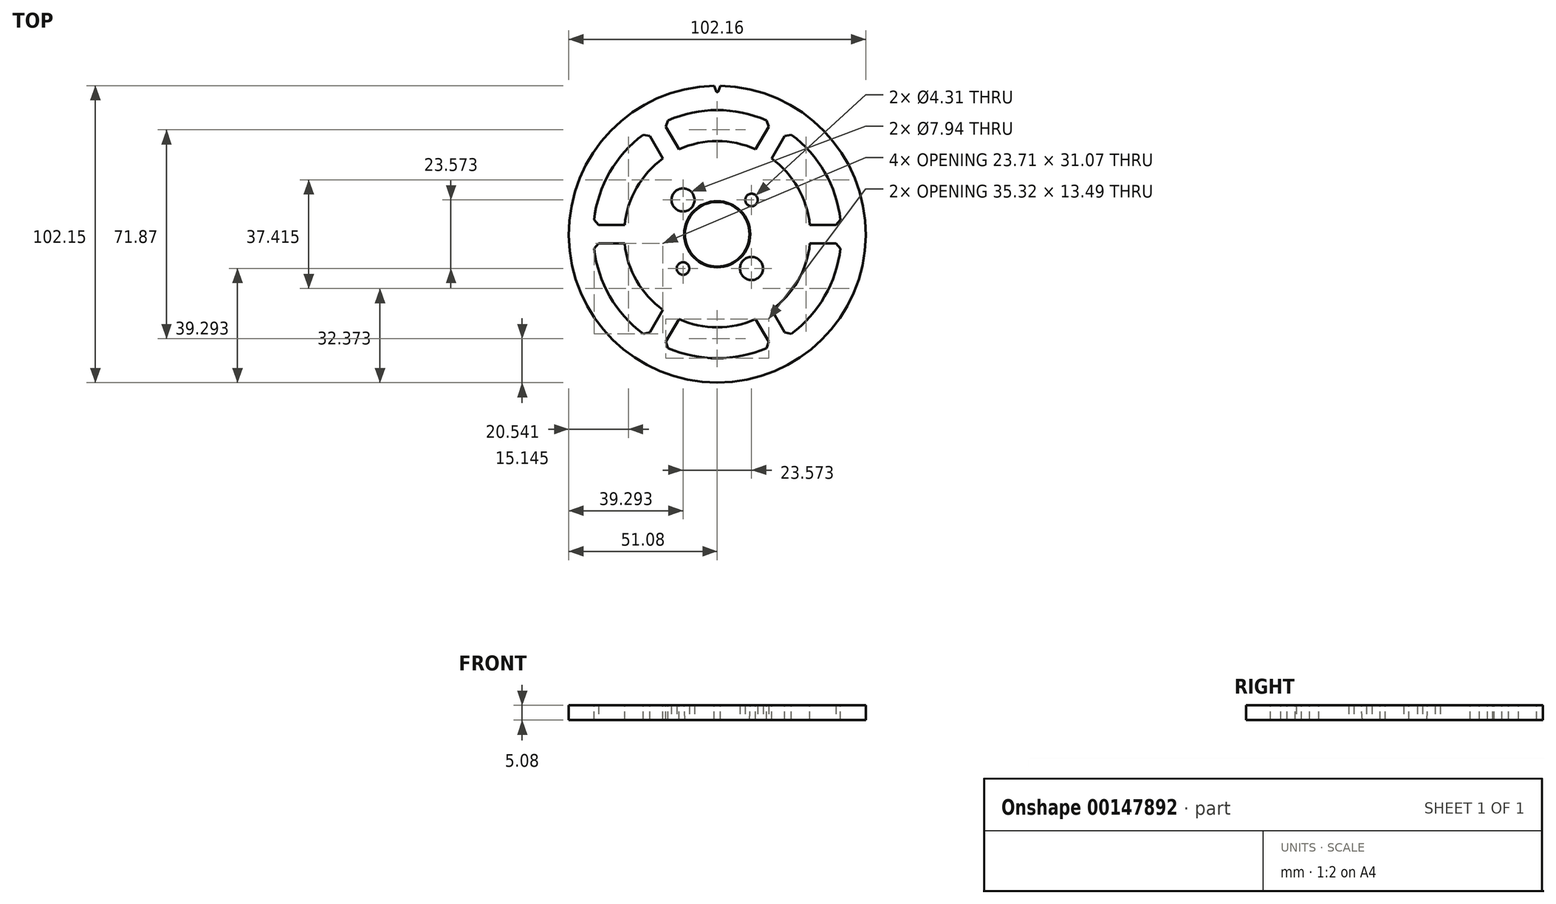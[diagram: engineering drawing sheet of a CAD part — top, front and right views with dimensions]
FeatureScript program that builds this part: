
annotation { "Feature Type Name" : "Feature", "Feature Type Description" : "" }
export const myFeature = defineFeature(function(context is Context, id is Id, definition is map)
    precondition{}
    {
        {
            var Q0;
            Q0=qCreatedBy(makeId("Top.planeOp"),FACE);
            var sketch = newSketch(context, id + "F0", { "sketchPlane" : qUnion([Q0])});
            skCircle(sketch, "E0", {"center": v(0, 0) * mm, "radius": 51.08 * mm});
            skCircle(sketch, "E1", {"center": v(0, 0) * mm, "radius": 11.11 * mm});
            skLineSegment(sketch, "E2.bottom", {"start": v(-11.79, -11.79) * mm, "end": v(11.79, -11.79) * mm, "construction": true});
            skLineSegment(sketch, "E2.top", {"start": v(-11.79, 11.79) * mm, "end": v(11.79, 11.79) * mm, "construction": true});
            skLineSegment(sketch, "E2.left", {"start": v(-11.79, -11.79) * mm, "end": v(-11.79, 11.79) * mm, "construction": true});
            skLineSegment(sketch, "E2.right", {"start": v(11.79, -11.79) * mm, "end": v(11.79, 11.79) * mm, "construction": true});
            skCircle(sketch, "E3", {"center": v(-11.79, -11.79) * mm, "radius": 5.56 * mm, "construction": true});
            skCircle(sketch, "E4", {"center": v(-11.79, -11.79) * mm, "radius": 2.15 * mm});
            skCircle(sketch, "E5", {"center": v(11.79, 11.79) * mm, "radius": 2.15 * mm});
            skCircle(sketch, "E6", {"center": v(11.79, -11.79) * mm, "radius": 3.97 * mm});
            skCircle(sketch, "E7", {"center": v(-11.79, 11.79) * mm, "radius": 3.97 * mm});
            skSolve(sketch);
        }
        {
            var Q0;
            Q0=makeQuery(id+"F0.imprint","IMPRINT",FACE,{"disambiguationData":[TD([[makeQuery(id+"F0.imprint","IMPRINT",EDGE,{"derivedFrom":sQuery(id+"F0.wireOp",EDGE,"d7zeTPih-CRss-xDOh-gPdP-rmPCdwzH7cdN.left")}),1.0]])]});
            var Q1;
            Q1=makeQuery(id+"F0.imprint","IMPRINT",FACE,{"disambiguationData":[TD([[makeQuery(id+"F0.imprint","IMPRINT",EDGE,{"derivedFrom":sQuery(id+"F0.wireOp",EDGE,"E0")}),1.0]])]});
            extrude(context, id + "F1", {"entities" : qUnion([Q0, Q1]), "depth" : 5.08 * mm});
        }
        {
            var Q0;
            Q0=makeQuery(id+"F1.opExtrude","CAP_FACE",FACE,{"disambiguationData":[OSD([sQuery(id+"F0.wireOp",EDGE,"d7zeTPih-CRss-xDOh-gPdP-rmPCdwzH7cdN.left"),sQuery(id+"F0.wireOp",EDGE,"d7zeTPih-CRss-xDOh-gPdP-rmPCdwzH7cdN.right"),sQuery(id+"F0.wireOp",EDGE,"ScfBMfkV-s1yN-Ls9R-SGr5-fEyGpD6zak8e"),sQuery(id+"F0.wireOp",EDGE,"xnxmVwjl-FvSF-m7sj-be2U-u85gZZGoORGZ"),sQuery(id+"F0.wireOp",EDGE,"E0")])],"isStart":false});
            var sketch = newSketch(context, id + "F2", { "sketchPlane" : qUnion([Q0])});
            skLineSegment(sketch, "E8", {"start": v(0, 0) * mm, "end": v(0, 51.08) * mm, "construction": true});
            skLineSegment(sketch, "E9", {"start": v(0, 0) * mm, "end": v(0.66, 51.07) * mm, "construction": true});
            skArc(sketch, "E10", {"start": v(1.02, 51.07) * mm, "mid": v(0, 51.08) * mm, "end": v(-1.02, 51.07) * mm});
            skLineSegment(sketch, "E11", {"start": v(-1.02, 51.07) * mm, "end": v(-0.28, 49.1) * mm});
            skLineSegment(sketch, "E12", {"start": v(1.02, 51.07) * mm, "end": v(0.28, 49.1) * mm});
            skPoint(sketch, "E13", {"position": v(0.65, 50.09) * mm});
            skArc(sketch, "E14", {"start": v(-0.28, 49.1) * mm, "mid": v(0, 48.91) * mm, "end": v(0.28, 49.1) * mm});
            skSolve(sketch);
        }
        {
            var Q0;
            Q0=qSketchRegion(id+"F2",true);
            var Q1;
            Q1=makeQuery(id+"F1.opExtrude","CAP_FACE",FACE,{"disambiguationData":[OSD([sQuery(id+"F0.wireOp",EDGE,"d7zeTPih-CRss-xDOh-gPdP-rmPCdwzH7cdN.left"),sQuery(id+"F0.wireOp",EDGE,"d7zeTPih-CRss-xDOh-gPdP-rmPCdwzH7cdN.right"),sQuery(id+"F0.wireOp",EDGE,"ScfBMfkV-s1yN-Ls9R-SGr5-fEyGpD6zak8e"),sQuery(id+"F0.wireOp",EDGE,"xnxmVwjl-FvSF-m7sj-be2U-u85gZZGoORGZ"),sQuery(id+"F0.wireOp",EDGE,"E0")])],"isStart":true});
            extrude(context, id + "F3", {"entities" : qUnion([Q0]), "operationType" : NewBodyOperationType.REMOVE, "endBound" : BoundingType.UP_TO_SURFACE, "oppositeDirection" : true, "endBoundEntityFace" : qUnion([Q1]), "depth" : 25.4 * mm});
        }
        {
            var Q0;
            Q0=makeQuery(id+"F1.opExtrude","CAP_FACE",FACE,{"disambiguationData":[OSD([sQuery(id+"F0.wireOp",EDGE,"E0"),sQuery(id+"F0.wireOp",EDGE,"E1"),sQuery(id+"F0.wireOp",EDGE,"E4"),sQuery(id+"F0.wireOp",EDGE,"E5"),sQuery(id+"F0.wireOp",EDGE,"E6"),sQuery(id+"F0.wireOp",EDGE,"E7")])],"isStart":false});
            var sketch = newSketch(context, id + "F4", { "sketchPlane" : qUnion([Q0])});
            skArc(sketch, "E15", {"start": v(-18.69, 26.01) * mm, "mid": v(-27.74, 16.01) * mm, "end": v(-31.87, 3.17) * mm});
            skLineSegment(sketch, "E16", {"start": v(0, 0) * mm, "end": v(-31.87, 0) * mm, "construction": true});
            skLineSegment(sketch, "E17", {"start": v(-31.87, 0) * mm, "end": v(-31.87, 3.17) * mm, "construction": true});
            skLineSegment(sketch, "E18", {"start": v(-31.87, 3.17) * mm, "end": v(-42.56, 3.17) * mm});
            skLineSegment(sketch, "E19", {"start": v(-42.56, 3.17) * mm, "end": v(-42.56, 0) * mm, "construction": true});
            skLineSegment(sketch, "E20", {"start": v(-42.56, 0) * mm, "end": v(-48.91, 0) * mm, "construction": true});
            skCircle(sketch, "E21", {"center": v(0, 0) * mm, "radius": 48.91 * mm, "construction": true});
            skLineSegment(sketch, "E22", {"start": v(0, 0) * mm, "end": v(-15.94, 27.6) * mm, "construction": true});
            skLineSegment(sketch, "E23", {"start": v(-18.69, 26.01) * mm, "end": v(-15.94, 27.6) * mm, "construction": true});
            skLineSegment(sketch, "E24", {"start": v(-18.69, 26.01) * mm, "end": v(-24.03, 35.27) * mm});
            skArc(sketch, "E25", {"start": v(-24.03, 35.27) * mm, "mid": v(-36.96, 21.34) * mm, "end": v(-42.56, 3.17) * mm});
            skSolve(sketch);
        }
        {
            var Q0;
            Q0=qSketchRegion(id+"F4",true);
            var Q1;
            Q1=makeQuery(id+"F1.opExtrude","CAP_FACE",FACE,{"disambiguationData":[OSD([sQuery(id+"F0.wireOp",EDGE,"E0"),sQuery(id+"F0.wireOp",EDGE,"E1"),sQuery(id+"F0.wireOp",EDGE,"E4"),sQuery(id+"F0.wireOp",EDGE,"E5"),sQuery(id+"F0.wireOp",EDGE,"E6"),sQuery(id+"F0.wireOp",EDGE,"E7")])],"isStart":true});
            extrude(context, id + "F5", {"entities" : qUnion([Q0]), "operationType" : NewBodyOperationType.REMOVE, "endBound" : BoundingType.UP_TO_SURFACE, "oppositeDirection" : true, "endBoundEntityFace" : qUnion([Q1]), "depth" : 25.4 * mm});
        }
        {
            var Q0;
            Q0=makeQuery(id+"F5.boolean.opBoolean","COPY",EDGE,{"derivedFrom":makeQuery(id+"F5.opExtrude","SWEPT_EDGE",EDGE,{"disambiguationData":[OSD([sQuery(id+"F4.wireOp",EDGE,"E24"),sQuery(id+"F4.wireOp",EDGE,"E25")])]})});
            var Q1;
            Q1=makeQuery(id+"F5.boolean.opBoolean","COPY",EDGE,{"derivedFrom":makeQuery(id+"F5.opExtrude","SWEPT_EDGE",EDGE,{"disambiguationData":[OSD([sQuery(id+"F4.wireOp",EDGE,"E18"),sQuery(id+"F4.wireOp",EDGE,"E25")])]})});
            chamfer(context, id + "F6", {"entities" : qUnion([Q0, Q1]), "width" : 1.59 * mm, "tangentPropagation" : true});
        }
        {
            var Q0;
            Q0=makeQuery(id+"F6.opChamfer","BLEND_FACE",FACE,{"disambiguationData":[OSD([sQuery(id+"F4.wireOp",EDGE,"E18"),sQuery(id+"F4.wireOp",EDGE,"E25")])]});
            var Q1;
            Q1=makeQuery(id+"F5.boolean.opBoolean","COPY",FACE,{"derivedFrom":makeQuery(id+"F5.opExtrude","SWEPT_FACE",FACE,{"disambiguationData":[OSD([sQuery(id+"F4.wireOp",EDGE,"E18")])]})});
            var Q2;
            Q2=makeQuery(id+"F6.opChamfer","BLEND_FACE",FACE,{"disambiguationData":[OSD([sQuery(id+"F4.wireOp",EDGE,"E15"),sQuery(id+"F4.wireOp",EDGE,"E18")])]});
            var Q3;
            Q3=makeQuery(id+"F5.boolean.opBoolean","COPY",FACE,{"derivedFrom":makeQuery(id+"F5.opExtrude","SWEPT_FACE",FACE,{"disambiguationData":[OSD([sQuery(id+"F4.wireOp",EDGE,"E25")])]})});
            var Q4;
            Q4=makeQuery(id+"F5.boolean.opBoolean","COPY",FACE,{"derivedFrom":makeQuery(id+"F5.opExtrude","SWEPT_FACE",FACE,{"disambiguationData":[OSD([sQuery(id+"F4.wireOp",EDGE,"E15")])]})});
            var Q5;
            Q5=makeQuery(id+"F6.opChamfer","BLEND_FACE",FACE,{"disambiguationData":[OSD([sQuery(id+"F4.wireOp",EDGE,"E15"),sQuery(id+"F4.wireOp",EDGE,"E24")])]});
            var Q6;
            Q6=makeQuery(id+"F5.boolean.opBoolean","COPY",FACE,{"derivedFrom":makeQuery(id+"F5.opExtrude","SWEPT_FACE",FACE,{"disambiguationData":[OSD([sQuery(id+"F4.wireOp",EDGE,"E24")])]})});
            var Q7;
            Q7=makeQuery(id+"F6.opChamfer","BLEND_FACE",FACE,{"disambiguationData":[OSD([sQuery(id+"F4.wireOp",EDGE,"E24"),sQuery(id+"F4.wireOp",EDGE,"E25")])]});
            var Q8;
            Q8=makeQuery(id+"F1.opExtrude","SWEPT_FACE",FACE,{"disambiguationData":[OSD([sQuery(id+"F0.wireOp",EDGE,"E1")])]});
            circularPattern(context, id + "F7", {"patternType" : PatternType.FACE, "faces" : qUnion([Q0, Q1, Q2, Q3, Q4, Q5, Q6, Q7]), "axis" : qUnion([Q8]), "angle" : 60 * degree, "instanceCount" : 6});
        }
        {
            var Q0;
            Q0=makeQuery(id+"F1.opExtrude","CAP_EDGE",EDGE,{"disambiguationData":[OSD([sQuery(id+"F0.wireOp",EDGE,"E1")])],"isStart":false});
            chamfer(context, id + "F8", {"entities" : qUnion([Q0]), "chamferType" : ChamferType.TWO_OFFSETS, "width1" : 5.08 * mm, "oppositeDirection" : false, "width2" : 0.25 * mm, "tangentPropagation" : true});
        }
    });
